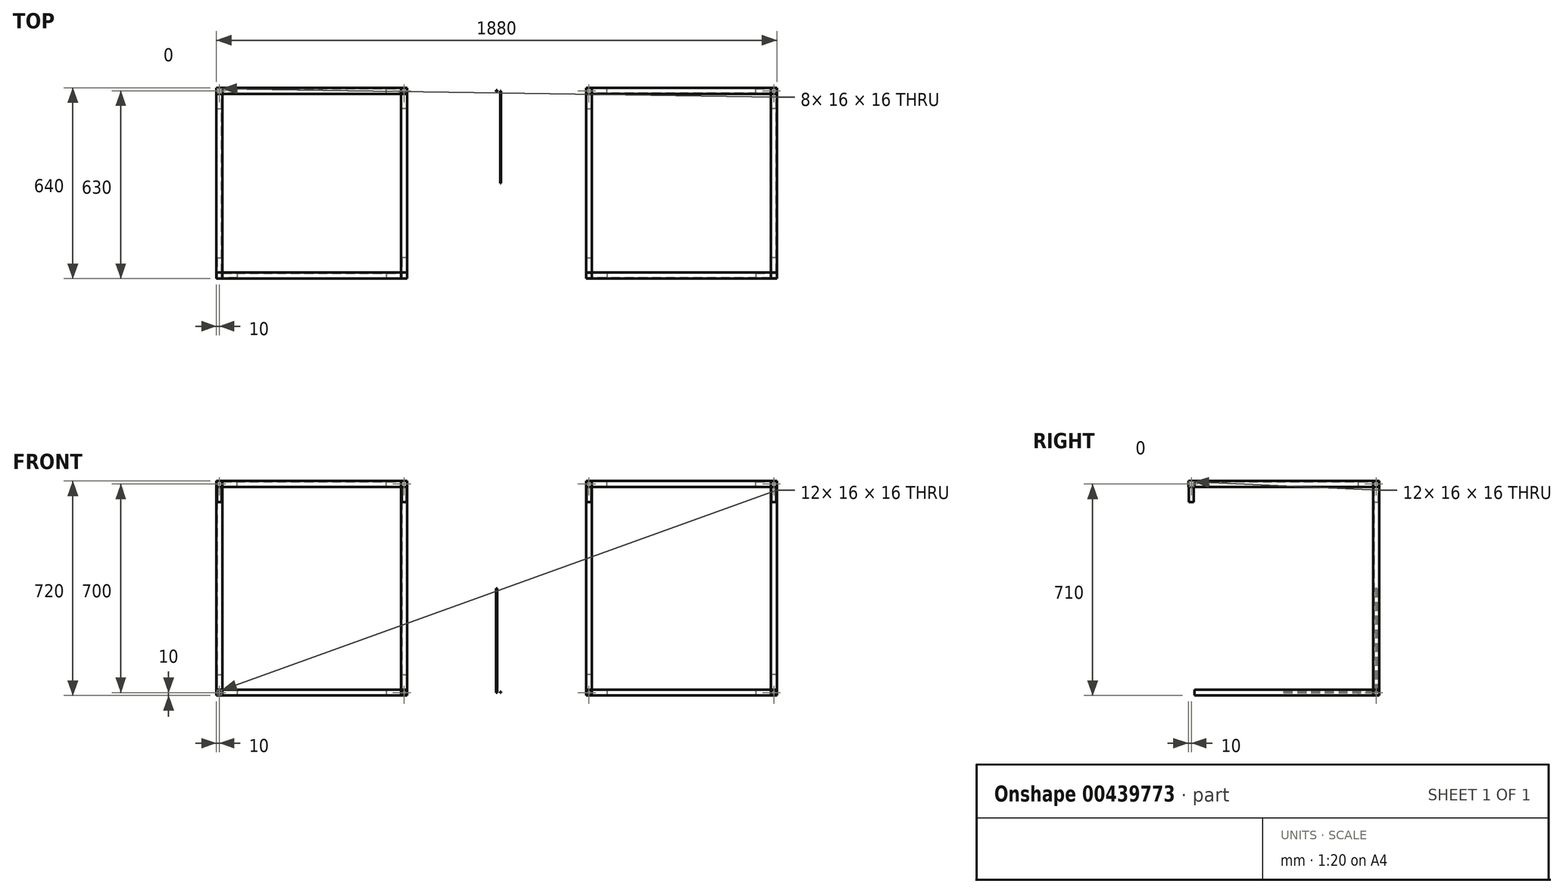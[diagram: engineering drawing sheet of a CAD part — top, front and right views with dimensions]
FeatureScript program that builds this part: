
annotation { "Feature Type Name" : "Feature", "Feature Type Description" : "" }
export const myFeature = defineFeature(function(context is Context, id is Id, definition is map)
    precondition{}
    {
        {
            var Q0;
            Q0=qCreatedBy(makeId("Front.planeOp"),FACE);
            var sketch = newSketch(context, id + "F0", { "sketchPlane" : qUnion([Q0])});
            skLineSegment(sketch, "E0", {"start": v(0, 0) * mm, "end": v(300, 0) * mm, "construction": true});
            skPoint(sketch, "E1", {"position": v(300, 0) * mm});
            skLineSegment(sketch, "E2.bottom", {"start": v(300, 10) * mm, "end": v(320, 10) * mm});
            skLineSegment(sketch, "E2.top", {"start": v(300, -10) * mm, "end": v(320, -10) * mm});
            skLineSegment(sketch, "E2.left", {"start": v(300, 10) * mm, "end": v(300, -10) * mm});
            skLineSegment(sketch, "E2.right", {"start": v(320, 10) * mm, "end": v(320, -10) * mm});
            skPoint(sketch, "E3", {"position": v(320, 0) * mm});
            skLineSegment(sketch, "E4", {"start": v(320, 0) * mm, "end": v(920, 0) * mm, "construction": true});
            skLineSegment(sketch, "E5.bottom", {"start": v(920, 10) * mm, "end": v(940, 10) * mm});
            skLineSegment(sketch, "E5.top", {"start": v(920, -10) * mm, "end": v(940, -10) * mm});
            skLineSegment(sketch, "E5.left", {"start": v(920, 10) * mm, "end": v(920, -10) * mm});
            skLineSegment(sketch, "E5.right", {"start": v(940, 10) * mm, "end": v(940, -10) * mm});
            skPoint(sketch, "E6", {"position": v(920, 0) * mm});
            skLineSegment(sketch, "E7", {"start": v(0, 0) * mm, "end": v(0, 700) * mm, "construction": true});
            skLineSegment(sketch, "E8", {"start": v(0, 700) * mm, "end": v(920, 700) * mm, "construction": true});
            skSolve(sketch);
        }
        {
            var Q0;
            Q0=makeQuery(id+"F0.imprint","IMPRINT",FACE,{"disambiguationData":[TD([[makeQuery(id+"F0.imprint","IMPRINT",EDGE,{"derivedFrom":sQuery(id+"F0.wireOp",EDGE,"e8899ceb-e48a-4a8d-9c5b-91becbcc4bf90.MirrorCS")}),1.0]])]});
            var Q1;
            Q1=makeQuery(id+"F0.imprint","IMPRINT",FACE,{"disambiguationData":[TD([[makeQuery(id+"F0.imprint","IMPRINT",EDGE,{"derivedFrom":sQuery(id+"F0.wireOp",EDGE,"e8899ceb-e48a-4a8d-9c5b-91becbcc4bf93.MirrorCS")}),1.0]])]});
            var Q2;
            Q2=makeQuery(id+"F0.imprint","IMPRINT",FACE,{"disambiguationData":[TD([[makeQuery(id+"F0.imprint","IMPRINT",EDGE,{"derivedFrom":sQuery(id+"F0.wireOp",EDGE,"E2.bottom")}),-1.0]])]});
            var Q3;
            Q3=makeQuery(id+"F0.imprint","IMPRINT",FACE,{"disambiguationData":[TD([[makeQuery(id+"F0.imprint","IMPRINT",EDGE,{"derivedFrom":sQuery(id+"F0.wireOp",EDGE,"E5.bottom")}),-1.0]])]});
            extrude(context, id + "F1", {"entities" : qUnion([Q0, Q1, Q2, Q3]), "endBound" : BoundingType.SYMMETRIC, "depth" : 20 * mm});
        }
        {
            var Q0;
            Q0=makeQuery(id+"F1.opExtrude","CAP_FACE",FACE,{"disambiguationData":[OSD([sQuery(id+"F0.wireOp",EDGE,"E2.bottom"),sQuery(id+"F0.wireOp",EDGE,"E2.top"),sQuery(id+"F0.wireOp",EDGE,"E2.left"),sQuery(id+"F0.wireOp",EDGE,"E2.right")])],"isStart":false});
            var sketch = newSketch(context, id + "F2", { "sketchPlane" : qUnion([Q0])});
            skLineSegment(sketch, "E9.0", {"start": v(302, 8) * mm, "end": v(318, 8) * mm});
            skLineSegment(sketch, "E9.1", {"start": v(302, 8) * mm, "end": v(302, -8) * mm});
            skLineSegment(sketch, "E9.2", {"start": v(302, -8) * mm, "end": v(318, -8) * mm});
            skLineSegment(sketch, "E9.3", {"start": v(318, 8) * mm, "end": v(318, -8) * mm});
            skSolve(sketch);
        }
        {
            var Q0;
            Q0=makeQuery(id+"F1.opExtrude","SWEPT_FACE",FACE,{"disambiguationData":[OSD([sQuery(id+"F0.wireOp",EDGE,"E2.right")])]});
            var sketch = newSketch(context, id + "F3", { "sketchPlane" : qUnion([Q0])});
            skLineSegment(sketch, "E10.0", {"start": v(-8, 8) * mm, "end": v(8, 8) * mm});
            skLineSegment(sketch, "E10.1", {"start": v(-8, 8) * mm, "end": v(-8, -8) * mm});
            skLineSegment(sketch, "E10.2", {"start": v(-8, -8) * mm, "end": v(8, -8) * mm});
            skLineSegment(sketch, "E10.3", {"start": v(8, 8) * mm, "end": v(8, -8) * mm});
            skSolve(sketch);
        }
        {
            var Q0;
            Q0=makeQuery(id+"F1.opExtrude","SWEPT_FACE",FACE,{"disambiguationData":[OSD([sQuery(id+"F0.wireOp",EDGE,"E2.bottom")])]});
            var sketch = newSketch(context, id + "F4", { "sketchPlane" : qUnion([Q0])});
            skLineSegment(sketch, "E11.0", {"start": v(318, 8) * mm, "end": v(302, 8) * mm});
            skLineSegment(sketch, "E11.1", {"start": v(318, -8) * mm, "end": v(318, 8) * mm});
            skLineSegment(sketch, "E11.2", {"start": v(302, -8) * mm, "end": v(318, -8) * mm});
            skLineSegment(sketch, "E11.3", {"start": v(302, 8) * mm, "end": v(302, -8) * mm});
            skSolve(sketch);
        }
        {
            var Q0;
            Q0=makeQuery(id+"F1.opExtrude","CAP_FACE",FACE,{"disambiguationData":[OSD([sQuery(id+"F0.wireOp",EDGE,"E5.bottom"),sQuery(id+"F0.wireOp",EDGE,"E5.top"),sQuery(id+"F0.wireOp",EDGE,"E5.left"),sQuery(id+"F0.wireOp",EDGE,"E5.right")])],"isStart":false});
            var sketch = newSketch(context, id + "F5", { "sketchPlane" : qUnion([Q0])});
            skLineSegment(sketch, "E12.0", {"start": v(922, 8) * mm, "end": v(922, -8) * mm});
            skLineSegment(sketch, "E12.1", {"start": v(938, 8) * mm, "end": v(922, 8) * mm});
            skLineSegment(sketch, "E12.2", {"start": v(938, -8) * mm, "end": v(938, 8) * mm});
            skLineSegment(sketch, "E12.3", {"start": v(922, -8) * mm, "end": v(938, -8) * mm});
            skSolve(sketch);
        }
        {
            var Q0;
            Q0=makeQuery(id+"F1.opExtrude","SWEPT_FACE",FACE,{"disambiguationData":[OSD([sQuery(id+"F0.wireOp",EDGE,"E5.left")])]});
            var sketch = newSketch(context, id + "F6", { "sketchPlane" : qUnion([Q0])});
            skLineSegment(sketch, "E13.0", {"start": v(-8, 8) * mm, "end": v(-8, -8) * mm});
            skLineSegment(sketch, "E13.1", {"start": v(8, 8) * mm, "end": v(-8, 8) * mm});
            skLineSegment(sketch, "E13.2", {"start": v(8, -8) * mm, "end": v(8, 8) * mm});
            skLineSegment(sketch, "E13.3", {"start": v(-8, -8) * mm, "end": v(8, -8) * mm});
            skSolve(sketch);
        }
        {
            var Q0;
            Q0=makeQuery(id+"F1.opExtrude","SWEPT_FACE",FACE,{"disambiguationData":[OSD([sQuery(id+"F0.wireOp",EDGE,"E5.bottom")])]});
            var sketch = newSketch(context, id + "F7", { "sketchPlane" : qUnion([Q0])});
            skLineSegment(sketch, "E14.0", {"start": v(938, 8) * mm, "end": v(922, 8) * mm});
            skLineSegment(sketch, "E14.1", {"start": v(938, -8) * mm, "end": v(938, 8) * mm});
            skLineSegment(sketch, "E14.2", {"start": v(922, -8) * mm, "end": v(938, -8) * mm});
            skLineSegment(sketch, "E14.3", {"start": v(922, 8) * mm, "end": v(922, -8) * mm});
            skSolve(sketch);
        }
        {
            var Q0;
            Q0=makeQuery(id+"F2.imprint","IMPRINT",FACE,{"disambiguationData":[TD([[makeQuery(id+"F2.imprint","IMPRINT",EDGE,{"derivedFrom":sQuery(id+"F2.wireOp",EDGE,"E9.0")}),-1.0]])]});
            var Q1;
            Q1=makeQuery(id+"F5.imprint","IMPRINT",FACE,{"disambiguationData":[TD([[makeQuery(id+"F5.imprint","IMPRINT",EDGE,{"derivedFrom":sQuery(id+"F5.wireOp",EDGE,"E12.0")}),1.0]])]});
            extrude(context, id + "F8", {"entities" : qUnion([Q0, Q1]), "operationType" : NewBodyOperationType.ADD, "depth" : 50 * mm});
        }
        {
            var Q0;
            Q0 = qSketchRegion(id + "F3", true);
            extrude(context, id + "F9", {"entities" : qUnion([Q0]), "operationType" : NewBodyOperationType.ADD, "depth" : 50 * mm});
        }
        {
            var Q0;
            Q0 = qSketchRegion(id + "F4", true);
            var Q1;
            Q1=makeQuery(id+"F7.imprint","IMPRINT",FACE,{"disambiguationData":[TD([[makeQuery(id+"F7.imprint","IMPRINT",EDGE,{"derivedFrom":sQuery(id+"F7.wireOp",EDGE,"E14.0")}),1.0]])]});
            extrude(context, id + "F10", {"entities" : qUnion([Q0, Q1]), "operationType" : NewBodyOperationType.ADD, "depth" : 50 * mm});
        }
        {
            var Q0;
            Q0=makeQuery(id+"F6.imprint","IMPRINT",FACE,{"disambiguationData":[TD([[makeQuery(id+"F6.imprint","IMPRINT",EDGE,{"derivedFrom":sQuery(id+"F6.wireOp",EDGE,"E13.0")}),1.0]])]});
            extrude(context, id + "F11", {"entities" : qUnion([Q0]), "operationType" : NewBodyOperationType.ADD, "depth" : 50 * mm});
        }
        {
            var Q0;
            Q0=makeQuery(id+"F1.opExtrude","SWEPT_FACE",FACE,{"disambiguationData":[OSD([sQuery(id+"F0.wireOp",EDGE,"E2.right")])]});
            extrude(context, id + "F12", {"entities" : qUnion([Q0]), "endBound" : BoundingType.UP_TO_NEXT, "depth" : 25 * mm});
        }
        {
            var Q0;
            Q0=makeQuery(id+"F1.opExtrude","CAP_FACE",FACE,{"disambiguationData":[OSD([sQuery(id+"F0.wireOp",EDGE,"E2.bottom"),sQuery(id+"F0.wireOp",EDGE,"E2.top"),sQuery(id+"F0.wireOp",EDGE,"E2.left"),sQuery(id+"F0.wireOp",EDGE,"E2.right")])],"isStart":false});
            var Q1;
            Q1=makeQuery(id+"F1.opExtrude","CAP_FACE",FACE,{"disambiguationData":[OSD([sQuery(id+"F0.wireOp",EDGE,"E5.bottom"),sQuery(id+"F0.wireOp",EDGE,"E5.top"),sQuery(id+"F0.wireOp",EDGE,"E5.left"),sQuery(id+"F0.wireOp",EDGE,"E5.right")])],"isStart":false});
            extrude(context, id + "F13", {"entities" : qUnion([Q0, Q1]), "depth" : 600 * mm});
        }
        {
            var Q0;
            Q0=qCreatedBy(makeId("Top.planeOp"),FACE);
            var sketch = newSketch(context, id + "F14", { "sketchPlane" : qUnion([Q0])});
            skLineSegment(sketch, "E15.bottom", {"start": v(2.35, 2.37) * mm, "end": v(-2.35, 2.37) * mm});
            skLineSegment(sketch, "E15.top", {"start": v(2.35, -2.37) * mm, "end": v(-2.35, -2.37) * mm});
            skLineSegment(sketch, "E15.left", {"start": v(2.35, 2.37) * mm, "end": v(2.35, -2.37) * mm});
            skLineSegment(sketch, "E15.right", {"start": v(-2.35, 2.37) * mm, "end": v(-2.35, -2.37) * mm});
            skPoint(sketch, "E15.middle", {"position": v(0, 0) * mm});
            skSolve(sketch);
        }
        {
            var Q0;
            Q0 = qSketchRegion(id + "F14", true);
            extrude(context, id + "F15", {"entities" : qUnion([Q0]), "depth" : 350 * mm});
        }
        {
            var Q0;
            Q0=makeQuery(id+"F1.opExtrude","SWEPT_FACE",FACE,{"disambiguationData":[OSD([sQuery(id+"F0.wireOp",EDGE,"E2.bottom")])]});
            var Q1;
            Q1=makeQuery(id+"F1.opExtrude","SWEPT_FACE",FACE,{"disambiguationData":[OSD([sQuery(id+"F0.wireOp",EDGE,"E5.bottom")])]});
            extrude(context, id + "F16", {"entities" : qUnion([Q0, Q1]), "depth" : 680 * mm});
        }
        {
            var Q0;
            Q0=makeQuery(id+"F13.opExtrude","SWEPT_BODY",BODY,{"disambiguationData":[OSD([sQuery(id+"F0.wireOp",EDGE,"E2.bottom"),sQuery(id+"F0.wireOp",EDGE,"E2.top"),sQuery(id+"F0.wireOp",EDGE,"E2.left"),sQuery(id+"F0.wireOp",EDGE,"E2.right")])]});
            var Q1;
            Q1=makeQuery(id+"F1.opExtrude","SWEPT_BODY",BODY,{"disambiguationData":[OSD([sQuery(id+"F0.wireOp",EDGE,"E2.bottom"),sQuery(id+"F0.wireOp",EDGE,"E2.top"),sQuery(id+"F0.wireOp",EDGE,"E2.left"),sQuery(id+"F0.wireOp",EDGE,"E2.right")])]});
            var Q2;
            Q2=makeQuery(id+"F12.opExtrude","SWEPT_BODY",BODY,{"disambiguationData":[OSD([sQuery(id+"F0.wireOp",EDGE,"E2.right")])]});
            var Q3;
            Q3=makeQuery(id+"F1.opExtrude","SWEPT_BODY",BODY,{"disambiguationData":[OSD([sQuery(id+"F0.wireOp",EDGE,"E5.bottom"),sQuery(id+"F0.wireOp",EDGE,"E5.top"),sQuery(id+"F0.wireOp",EDGE,"E5.left"),sQuery(id+"F0.wireOp",EDGE,"E5.right")])]});
            var Q4;
            Q4=makeQuery(id+"F13.opExtrude","SWEPT_BODY",BODY,{"disambiguationData":[OSD([sQuery(id+"F0.wireOp",EDGE,"E5.bottom"),sQuery(id+"F0.wireOp",EDGE,"E5.top"),sQuery(id+"F0.wireOp",EDGE,"E5.left"),sQuery(id+"F0.wireOp",EDGE,"E5.right")])]});
            var Q5;
            Q5=makeQuery(id+"F15.opExtrude","CAP_FACE",FACE,{"disambiguationData":[OSD([sQuery(id+"F14.wireOp",EDGE,"E15.bottom"),sQuery(id+"F14.wireOp",EDGE,"E15.top"),sQuery(id+"F14.wireOp",EDGE,"E15.left"),sQuery(id+"F14.wireOp",EDGE,"E15.right")])],"isStart":false});
            mirror(context, id + "F17", {"entities" : qUnion([Q0, Q1, Q2, Q3, Q4]), "mirrorPlane" : qUnion([Q5])});
        }
        {
            var Q0;
            Q0=makeQuery(id+"F1.opExtrude","SWEPT_BODY",BODY,{"disambiguationData":[OSD([sQuery(id+"F0.wireOp",EDGE,"E5.bottom"),sQuery(id+"F0.wireOp",EDGE,"E5.top"),sQuery(id+"F0.wireOp",EDGE,"E5.left"),sQuery(id+"F0.wireOp",EDGE,"E5.right")])]});
            var Q1;
            Q1=makeQuery(id+"F17.opPattern","COPY",BODY,{"derivedFrom":makeQuery(id+"F1.opExtrude","SWEPT_BODY",BODY,{"disambiguationData":[OSD([sQuery(id+"F0.wireOp",EDGE,"E5.bottom"),sQuery(id+"F0.wireOp",EDGE,"E5.top"),sQuery(id+"F0.wireOp",EDGE,"E5.left"),sQuery(id+"F0.wireOp",EDGE,"E5.right")])]}),"instanceName":"1"});
            var Q2;
            Q2=makeQuery(id+"F17.opPattern","COPY",BODY,{"derivedFrom":makeQuery(id+"F13.opExtrude","SWEPT_BODY",BODY,{"disambiguationData":[OSD([sQuery(id+"F0.wireOp",EDGE,"E5.bottom"),sQuery(id+"F0.wireOp",EDGE,"E5.top"),sQuery(id+"F0.wireOp",EDGE,"E5.left"),sQuery(id+"F0.wireOp",EDGE,"E5.right")])]}),"instanceName":"1"});
            var Q3;
            Q3=makeQuery(id+"F17.opPattern","COPY",BODY,{"derivedFrom":makeQuery(id+"F1.opExtrude","SWEPT_BODY",BODY,{"disambiguationData":[OSD([sQuery(id+"F0.wireOp",EDGE,"E2.bottom"),sQuery(id+"F0.wireOp",EDGE,"E2.top"),sQuery(id+"F0.wireOp",EDGE,"E2.left"),sQuery(id+"F0.wireOp",EDGE,"E2.right")])]}),"instanceName":"1"});
            var Q4;
            Q4=makeQuery(id+"F17.opPattern","COPY",BODY,{"derivedFrom":makeQuery(id+"F12.opExtrude","SWEPT_BODY",BODY,{"disambiguationData":[OSD([sQuery(id+"F0.wireOp",EDGE,"E2.right")])]}),"instanceName":"1"});
            var Q5;
            Q5=makeQuery(id+"F17.opPattern","COPY",BODY,{"derivedFrom":makeQuery(id+"F13.opExtrude","SWEPT_BODY",BODY,{"disambiguationData":[OSD([sQuery(id+"F0.wireOp",EDGE,"E2.bottom"),sQuery(id+"F0.wireOp",EDGE,"E2.top"),sQuery(id+"F0.wireOp",EDGE,"E2.left"),sQuery(id+"F0.wireOp",EDGE,"E2.right")])]}),"instanceName":"1"});
            var Q6;
            Q6=makeQuery(id+"F16.opExtrude","SWEPT_BODY",BODY,{"disambiguationData":[OSD([sQuery(id+"F0.wireOp",EDGE,"E5.bottom")])]});
            var Q7;
            Q7=makeQuery(id+"F16.opExtrude","SWEPT_BODY",BODY,{"disambiguationData":[OSD([sQuery(id+"F0.wireOp",EDGE,"E2.bottom")])]});
            var Q8;
            Q8=makeQuery(id+"F12.opExtrude","SWEPT_BODY",BODY,{"disambiguationData":[OSD([sQuery(id+"F0.wireOp",EDGE,"E2.right")])]});
            var Q9;
            Q9=makeQuery(id+"F13.opExtrude","SWEPT_BODY",BODY,{"disambiguationData":[OSD([sQuery(id+"F0.wireOp",EDGE,"E5.bottom"),sQuery(id+"F0.wireOp",EDGE,"E5.top"),sQuery(id+"F0.wireOp",EDGE,"E5.left"),sQuery(id+"F0.wireOp",EDGE,"E5.right")])]});
            var Q10;
            Q10=makeQuery(id+"F13.opExtrude","SWEPT_BODY",BODY,{"disambiguationData":[OSD([sQuery(id+"F0.wireOp",EDGE,"E2.bottom"),sQuery(id+"F0.wireOp",EDGE,"E2.top"),sQuery(id+"F0.wireOp",EDGE,"E2.left"),sQuery(id+"F0.wireOp",EDGE,"E2.right")])]});
            var Q11;
            Q11=makeQuery(id+"F1.opExtrude","SWEPT_BODY",BODY,{"disambiguationData":[OSD([sQuery(id+"F0.wireOp",EDGE,"E2.bottom"),sQuery(id+"F0.wireOp",EDGE,"E2.top"),sQuery(id+"F0.wireOp",EDGE,"E2.left"),sQuery(id+"F0.wireOp",EDGE,"E2.right")])]});
            var Q12;
            Q12=qCreatedBy(makeId("Right.planeOp"),FACE);
            mirror(context, id + "F18", {"entities" : qUnion([Q0, Q1, Q2, Q3, Q4, Q5, Q6, Q7, Q8, Q9, Q10, Q11]), "mirrorPlane" : qUnion([Q12])});
        }
        {
            var Q0;
            Q0=qCreatedBy(makeId("Front.planeOp"),FACE);
            var sketch = newSketch(context, id + "F19", { "sketchPlane" : qUnion([Q0])});
            skLineSegment(sketch, "E16.bottom", {"start": v(12.1, 0) * mm, "end": v(14.64, 0) * mm});
            skLineSegment(sketch, "E16.top", {"start": v(12.1, 3.57) * mm, "end": v(14.64, 3.57) * mm});
            skLineSegment(sketch, "E16.left", {"start": v(12.1, 0) * mm, "end": v(12.1, 3.57) * mm});
            skLineSegment(sketch, "E16.right", {"start": v(14.64, 0) * mm, "end": v(14.64, 3.57) * mm});
            skSolve(sketch);
        }
        {
            var Q0;
            Q0 = qSketchRegion(id + "F19", true);
            extrude(context, id + "F20", {"entities" : qUnion([Q0]), "depth" : 310 * mm});
        }
        {
            var Q0;
            Q0=makeQuery(id+"F17.opPattern","COPY",BODY,{"derivedFrom":makeQuery(id+"F12.opExtrude","SWEPT_BODY",BODY,{"disambiguationData":[OSD([sQuery(id+"F0.wireOp",EDGE,"E2.right")])]}),"instanceName":"1"});
            var Q1;
            Q1=makeQuery(id+"F17.opPattern","COPY",BODY,{"derivedFrom":makeQuery(id+"F1.opExtrude","SWEPT_BODY",BODY,{"disambiguationData":[OSD([sQuery(id+"F0.wireOp",EDGE,"E2.bottom"),sQuery(id+"F0.wireOp",EDGE,"E2.top"),sQuery(id+"F0.wireOp",EDGE,"E2.left"),sQuery(id+"F0.wireOp",EDGE,"E2.right")])]}),"instanceName":"1"});
            var Q2;
            Q2=makeQuery(id+"F17.opPattern","COPY",BODY,{"derivedFrom":makeQuery(id+"F1.opExtrude","SWEPT_BODY",BODY,{"disambiguationData":[OSD([sQuery(id+"F0.wireOp",EDGE,"E5.bottom"),sQuery(id+"F0.wireOp",EDGE,"E5.top"),sQuery(id+"F0.wireOp",EDGE,"E5.left"),sQuery(id+"F0.wireOp",EDGE,"E5.right")])]}),"instanceName":"1"});
            var Q3;
            Q3=makeQuery(id+"F18.opPattern","COPY",BODY,{"derivedFrom":makeQuery(id+"F17.opPattern","COPY",BODY,{"derivedFrom":makeQuery(id+"F12.opExtrude","SWEPT_BODY",BODY,{"disambiguationData":[OSD([sQuery(id+"F0.wireOp",EDGE,"E2.right")])]}),"instanceName":"1"}),"instanceName":"1"});
            var Q4;
            Q4=makeQuery(id+"F18.opPattern","COPY",BODY,{"derivedFrom":makeQuery(id+"F17.opPattern","COPY",BODY,{"derivedFrom":makeQuery(id+"F1.opExtrude","SWEPT_BODY",BODY,{"disambiguationData":[OSD([sQuery(id+"F0.wireOp",EDGE,"E2.bottom"),sQuery(id+"F0.wireOp",EDGE,"E2.top"),sQuery(id+"F0.wireOp",EDGE,"E2.left"),sQuery(id+"F0.wireOp",EDGE,"E2.right")])]}),"instanceName":"1"}),"instanceName":"1"});
            var Q5;
            Q5=makeQuery(id+"F18.opPattern","COPY",BODY,{"derivedFrom":makeQuery(id+"F17.opPattern","COPY",BODY,{"derivedFrom":makeQuery(id+"F1.opExtrude","SWEPT_BODY",BODY,{"disambiguationData":[OSD([sQuery(id+"F0.wireOp",EDGE,"E5.bottom"),sQuery(id+"F0.wireOp",EDGE,"E5.top"),sQuery(id+"F0.wireOp",EDGE,"E5.left"),sQuery(id+"F0.wireOp",EDGE,"E5.right")])]}),"instanceName":"1"}),"instanceName":"1"});
            var Q6;
            Q6=makeQuery(id+"F20.opExtrude","CAP_FACE",FACE,{"disambiguationData":[OSD([sQuery(id+"F19.wireOp",EDGE,"E16.bottom"),sQuery(id+"F19.wireOp",EDGE,"E16.top"),sQuery(id+"F19.wireOp",EDGE,"E16.left"),sQuery(id+"F19.wireOp",EDGE,"E16.right")])],"isStart":false});
            mirror(context, id + "F21", {"entities" : qUnion([Q0, Q1, Q2, Q3, Q4, Q5]), "mirrorPlane" : qUnion([Q6])});
        }
    });
